# Revit family: 879-002X99-001-DN65-250
name_source: partatom
category: Pipe Accessories
units: mm (PartAtom-declared; Revit-internal decimal feet)

## family parameters
Always vertical = Yes
Cut with Voids When Loaded = No
Part Type = Valve - Breaks Into
Round Connector Dimension = Use Diameter
Shared = No
Work Plane-Based = No

## types (48) — shared parameters
879-0065-00-14400209999 = DN65_PN10/16
879-0065-00-144002099A0 = DN65_PN10/16
879-0065-00-14400219999 = DN65_PN10/16
879-0065-00-144002199A0 = DN65_PN10/16
879-0065-00-14400229999 = DN65_PN10/16
879-0065-00-144002299A0 = DN65_PN10/16
879-0080-00-14400209999 = DN80_PN10/16
879-0080-00-144002099A0 = DN80_PN10/16
879-0080-00-14400219999 = DN80_PN10/16
879-0080-00-144002199A0 = DN80_PN10/16
879-0080-00-14400229999 = DN80_PN10/16
879-0080-00-144002299A0 = DN80_PN10/16
879-0100-00-14400209999 = DN100_PN10/16
879-0100-00-144002099A0 = DN100_PN10/16
879-0100-00-14400219999 = DN100_PN10/16
879-0100-00-144002199A0 = DN100_PN10/16
879-0100-00-14400229990 = DN100_PN10/16
879-0100-00-144002299A0 = DN100_PN10/16
879-0125-00-14400209999 = DN125_PN10/16
879-0125-00-144002099A0 = DN125_PN10/16
879-0125-00-14400219990 = DN125_PN10/16
879-0125-00-144002199A0 = DN125_PN10/16
879-0125-00-14400229999 = DN125_PN10/16
879-0125-00-144002299A0 = DN125_PN10/16
879-0150-00-14400209999 = DN150_PN10/16
879-0150-00-144002099A0 = DN150_PN10/16
879-0150-00-14400219999 = DN150_PN10/16
879-0150-00-144002199A0 = DN150_PN10/16
879-0150-00-14400229999 = DN150_PN10/16
879-0150-00-144002299A0 = DN150_PN10/16
879-0150-00-14400239999 = DN150_PN10/16
879-0150-00-144002399A0 = DN150_PN10/16
879-0200-00-14400209999 = DN200_PN16
879-0200-00-144002099A0 = DN200_PN16
879-0200-00-14400219999 = DN200_PN16
879-0200-00-144002199A0 = DN200_PN16
879-0200-00-14400229999 = DN200_PN16
879-0200-00-144002299A0 = DN200_PN16
879-0200-00-14400239999 = DN200_PN16
879-0200-00-144002399A0 = DN200_PN16
879-0250-00-14400209999 = DN250_PN16
879-0250-00-144002099A0 = DN250_PN16
879-0250-00-14400219999 = DN250_PN16
879-0250-00-144002199A0 = DN250_PN16
879-0250-00-14400229999 = DN250_PN16
879-0250-00-144002299A0 = DN250_PN16
879-0250-00-14400239999 = DN250_PN16
879-0250-00-144002399A0 = DN250_PN16
Body_wall_thickness = 10 mm  [stored 0.0328084 ft]
Description_ = AVK CONSTANT FLOW CONTROL VALVE
Search_Table = 879-002X99-001-DN65-250
URL product pages = https://www.avkvalves.com

## per-type parameters (varying)
- 879-0065-00-14400209999_DN65_PN10/16: Body_Collar_Dia=30.21 mm; Body_Collar_Dia_2=26.01 mm; Body_Flange_Dia=93.55 mm; Body_Flange_Dia_2=103.57 mm; Body_Height_1=72.5 mm; Body_Height_2=36.25 mm; Body_Height_3=58 mm; Body_Height_4=51.25 mm; Body_Top_Dia=13 mm; Body_Top_Dia_2=10.84 mm; Body_With_Dia=72.5 mm; Body_With_Dia_2=78.38 mm; Bolt_support=193.33 mm; Bolt_support_2=96.67 mm; Bolt_support_Dia=12 mm  [stored 0.0393701 ft]; Bolt_support_lenght=52.5 mm; Bolt_support_lenght_2=62.5 mm; Bottom_profile=16.25 mm  [stored 0.0533136 ft]; D1=59 mm; DN=65 mm; FOD=92.5 mm; Fillet_Length=6 mm  [stored 0.019685 ft]; Flange_thickness=19 mm; H3=420 mm; ID=32.5 mm; L=290 mm; L1=307 mm; L_Ref=298.5 mm; PG_Dia=32.5 mm; PG_Ref=48.33 mm; PG_depth=8.4 mm  [stored 0.0275591 ft]; PG_ref=42.5 mm; Pilot_Dia_1=17.5 mm; Pilot_Dia_2=35 mm; Pilot_Dia_3=11.67 mm; Pilot_Dia_4=5.83 mm; Pilot_Dia_5=3.89 mm; Pilot_top_1=264.63 mm; Pilot_top_ref=62.88 mm; Profile1_Height=152 mm; Profile1_Length=25 mm; Profile1_Length_2=16.67 mm; Profile_Dia=6 mm  [stored 0.019685 ft]; Profile_Dia_2=6 mm  [stored 0.019685 ft]; Profile_Dia_3=12 mm  [stored 0.0393701 ft]; Top_Profile=116 mm; Top_Profile_Ref=121 mm; Top_Ref=201.75 mm; Top_Ref_2=233.19 mm; W=255 mm; W_Ref=252 mm
- 879-0065-00-144002099A0_DN65_PN10/16: Body_Collar_Dia=30.21 mm; Body_Collar_Dia_2=26.01 mm; Body_Flange_Dia=93.55 mm; Body_Flange_Dia_2=103.57 mm; Body_Height_1=72.5 mm; Body_Height_2=36.25 mm; Body_Height_3=72.5 mm; Body_Height_4=51.25 mm; Body_Top_Dia=13 mm; Body_Top_Dia_2=10.84 mm; Body_With_Dia=72.5 mm; Body_With_Dia_2=78.38 mm; Bolt_support=193.33 mm; Bolt_support_2=96.67 mm; Bolt_support_Dia=12 mm  [stored 0.0393701 ft]; Bolt_support_lenght=52.55 mm; Bolt_support_lenght_2=62.55 mm; Bottom_profile=16.28 mm; D1=59 mm; DN=65.1 mm; FOD=92.5 mm; Fillet_Length=6 mm  [stored 0.019685 ft]; Flange_thickness=19 mm; H3=420 mm; ID=32.55 mm; L=290 mm; L1=307 mm; L_Ref=298.5 mm; PG_Dia=32.55 mm; PG_Ref=48.33 mm; PG_depth=8.4 mm  [stored 0.0275591 ft]; PG_ref=42.55 mm; Pilot_Dia_1=17.5 mm; Pilot_Dia_2=35 mm; Pilot_Dia_3=11.67 mm; Pilot_Dia_4=5.83 mm; Pilot_Dia_5=3.89 mm; Pilot_top_1=271.88 mm; Pilot_top_ref=55.63 mm; Profile1_Height=170 mm; Profile1_Length=25 mm; Profile1_Length_2=16.67 mm; Profile_Dia=6 mm  [stored 0.019685 ft]; Profile_Dia_2=6 mm  [stored 0.019685 ft]; Profile_Dia_3=12 mm  [stored 0.0393701 ft]; Top_Profile=116 mm; Top_Profile_Ref=121 mm; Top_Ref=216.25 mm; Top_Ref_2=244.06 mm; W=255 mm; W_Ref=252 mm
- 879-0065-00-14400219999_DN65_PN10/16: Body_Collar_Dia=30.21 mm; Body_Collar_Dia_2=26.01 mm; Body_Flange_Dia=93.55 mm; Body_Flange_Dia_2=103.57 mm; Body_Height_1=72.5 mm; Body_Height_2=36.25 mm; Body_Height_3=58 mm; Body_Height_4=51.25 mm; Body_Top_Dia=13 mm; Body_Top_Dia_2=10.84 mm; Body_With_Dia=72.5 mm; Body_With_Dia_2=78.38 mm; Bolt_support=193.33 mm; Bolt_support_2=96.67 mm; Bolt_support_Dia=12 mm  [stored 0.0393701 ft]; Bolt_support_lenght=52.6 mm; Bolt_support_lenght_2=62.6 mm; Bottom_profile=16.3 mm; D1=59 mm; DN=65.2 mm; FOD=92.5 mm; Fillet_Length=6 mm  [stored 0.019685 ft]; Flange_thickness=19 mm; H3=420 mm; ID=32.6 mm; L=290 mm; L1=307 mm; L_Ref=298.5 mm; PG_Dia=32.6 mm; PG_Ref=48.33 mm; PG_depth=8.4 mm  [stored 0.0275591 ft]; PG_ref=42.6 mm; Pilot_Dia_1=17.5 mm; Pilot_Dia_2=35 mm; Pilot_Dia_3=11.67 mm; Pilot_Dia_4=5.83 mm; Pilot_Dia_5=3.89 mm; Pilot_top_1=264.63 mm; Pilot_top_ref=62.88 mm; Profile1_Height=152 mm; Profile1_Length=25 mm; Profile1_Length_2=16.67 mm; Profile_Dia=6 mm  [stored 0.019685 ft]; Profile_Dia_2=6 mm  [stored 0.019685 ft]; Profile_Dia_3=12 mm  [stored 0.0393701 ft]; Top_Profile=116 mm; Top_Profile_Ref=121 mm; Top_Ref=201.75 mm; Top_Ref_2=233.19 mm; W=255 mm; W_Ref=252 mm
- 879-0065-00-144002199A0_DN65_PN10/16: Body_Collar_Dia=30.21 mm; Body_Collar_Dia_2=26.01 mm; Body_Flange_Dia=93.55 mm; Body_Flange_Dia_2=103.57 mm; Body_Height_1=72.5 mm; Body_Height_2=36.25 mm; Body_Height_3=72.5 mm; Body_Height_4=51.25 mm; Body_Top_Dia=13 mm; Body_Top_Dia_2=10.84 mm; Body_With_Dia=72.5 mm; Body_With_Dia_2=78.38 mm; Bolt_support=193.33 mm; Bolt_support_2=96.67 mm; Bolt_support_Dia=12 mm  [stored 0.0393701 ft]; Bolt_support_lenght=52.65 mm; Bolt_support_lenght_2=62.65 mm; Bottom_profile=16.33 mm; D1=59 mm; DN=65.3 mm; FOD=92.5 mm; Fillet_Length=6 mm  [stored 0.019685 ft]; Flange_thickness=19 mm; H3=420 mm; ID=32.65 mm; L=290 mm; L1=307 mm; L_Ref=298.5 mm; PG_Dia=32.65 mm; PG_Ref=48.33 mm; PG_depth=8.4 mm  [stored 0.0275591 ft]; PG_ref=42.65 mm; Pilot_Dia_1=17.5 mm; Pilot_Dia_2=35 mm; Pilot_Dia_3=11.67 mm; Pilot_Dia_4=5.83 mm; Pilot_Dia_5=3.89 mm; Pilot_top_1=271.88 mm; Pilot_top_ref=55.63 mm; Profile1_Height=170 mm; Profile1_Length=25 mm; Profile1_Length_2=16.67 mm; Profile_Dia=6 mm  [stored 0.019685 ft]; Profile_Dia_2=6 mm  [stored 0.019685 ft]; Profile_Dia_3=12 mm  [stored 0.0393701 ft]; Top_Profile=116 mm; Top_Profile_Ref=121 mm; Top_Ref=216.25 mm; Top_Ref_2=244.06 mm; W=255 mm; W_Ref=252 mm
- 879-0065-00-14400229999_DN65_PN10/16: Body_Collar_Dia=30.21 mm; Body_Collar_Dia_2=26.01 mm; Body_Flange_Dia=93.55 mm; Body_Flange_Dia_2=103.57 mm; Body_Height_1=72.5 mm; Body_Height_2=36.25 mm; Body_Height_3=58 mm; Body_Height_4=51.25 mm; Body_Top_Dia=13 mm; Body_Top_Dia_2=10.84 mm; Body_With_Dia=72.5 mm; Body_With_Dia_2=78.38 mm; Bolt_support=193.33 mm; Bolt_support_2=96.67 mm; Bolt_support_Dia=12 mm  [stored 0.0393701 ft]; Bolt_support_lenght=52.7 mm; Bolt_support_lenght_2=62.7 mm; Bottom_profile=16.35 mm  [stored 0.0536417 ft]; D1=59 mm; DN=65.4 mm; FOD=92.5 mm; Fillet_Length=6 mm  [stored 0.019685 ft]; Flange_thickness=19 mm; H3=420 mm; ID=32.7 mm; L=290 mm; L1=307 mm; L_Ref=298.5 mm; PG_Dia=32.7 mm; PG_Ref=48.33 mm; PG_depth=8.4 mm  [stored 0.0275591 ft]; PG_ref=42.7 mm; Pilot_Dia_1=17.5 mm; Pilot_Dia_2=35 mm; Pilot_Dia_3=11.67 mm; Pilot_Dia_4=5.83 mm; Pilot_Dia_5=3.89 mm; Pilot_top_1=264.63 mm; Pilot_top_ref=62.88 mm; Profile1_Height=152 mm; Profile1_Length=25 mm; Profile1_Length_2=16.67 mm; Profile_Dia=6 mm  [stored 0.019685 ft]; Profile_Dia_2=6 mm  [stored 0.019685 ft]; Profile_Dia_3=12 mm  [stored 0.0393701 ft]; Top_Profile=116 mm; Top_Profile_Ref=121 mm; Top_Ref=201.75 mm; Top_Ref_2=233.19 mm; W=255 mm; W_Ref=252 mm
- 879-0065-00-144002299A0_DN65_PN10/16: Body_Collar_Dia=30.21 mm; Body_Collar_Dia_2=26.01 mm; Body_Flange_Dia=93.55 mm; Body_Flange_Dia_2=103.57 mm; Body_Height_1=72.5 mm; Body_Height_2=36.25 mm; Body_Height_3=72.5 mm; Body_Height_4=51.25 mm; Body_Top_Dia=13 mm; Body_Top_Dia_2=10.84 mm; Body_With_Dia=72.5 mm; Body_With_Dia_2=78.38 mm; Bolt_support=193.33 mm; Bolt_support_2=96.67 mm; Bolt_support_Dia=12 mm  [stored 0.0393701 ft]; Bolt_support_lenght=52.75 mm; Bolt_support_lenght_2=62.75 mm; Bottom_profile=16.38 mm; D1=59 mm; DN=65.5 mm; FOD=92.5 mm; Fillet_Length=6 mm  [stored 0.019685 ft]; Flange_thickness=19 mm; H3=420 mm; ID=32.75 mm; L=290 mm; L1=307 mm; L_Ref=298.5 mm; PG_Dia=32.75 mm; PG_Ref=48.33 mm; PG_depth=8.4 mm  [stored 0.0275591 ft]; PG_ref=42.75 mm; Pilot_Dia_1=17.5 mm; Pilot_Dia_2=35 mm; Pilot_Dia_3=11.67 mm; Pilot_Dia_4=5.83 mm; Pilot_Dia_5=3.89 mm; Pilot_top_1=271.88 mm; Pilot_top_ref=55.63 mm; Profile1_Height=170 mm; Profile1_Length=25 mm; Profile1_Length_2=16.67 mm; Profile_Dia=6 mm  [stored 0.019685 ft]; Profile_Dia_2=6 mm  [stored 0.019685 ft]; Profile_Dia_3=12 mm  [stored 0.0393701 ft]; Top_Profile=116 mm; Top_Profile_Ref=121 mm; Top_Ref=216.25 mm; Top_Ref_2=244.06 mm; W=255 mm; W_Ref=252 mm
- 879-0080-00-14400209999_DN80_PN10/16: Body_Collar_Dia=32.29 mm; Body_Collar_Dia_2=27.8 mm; Body_Flange_Dia=100 mm; Body_Flange_Dia_2=110.71 mm; Body_Height_1=77.5 mm; Body_Height_2=38.75 mm; Body_Height_3=62 mm; Body_Height_4=53.75 mm; Body_Top_Dia=13.9 mm; Body_Top_Dia_2=11.58 mm; Body_With_Dia=77.5 mm; Body_With_Dia_2=83.78 mm; Bolt_support=206.67 mm; Bolt_support_2=103.33 mm; Bolt_support_Dia=12 mm  [stored 0.0393701 ft]; Bolt_support_lenght=60 mm; Bolt_support_lenght_2=70 mm; Bottom_profile=20 mm; D1=66 mm; DN=80 mm; FOD=100 mm; Fillet_Length=6 mm  [stored 0.019685 ft]; Flange_thickness=19 mm; H3=435 mm; ID=40 mm; L=310 mm; L1=327 mm; L_Ref=318.5 mm; PG_Dia=40 mm; PG_Ref=51.67 mm; PG_depth=8.4 mm  [stored 0.0275591 ft]; PG_ref=50 mm; Pilot_Dia_1=19.5 mm; Pilot_Dia_2=39 mm; Pilot_Dia_3=13 mm; Pilot_Dia_4=6.5 mm; Pilot_Dia_5=4.33 mm; Pilot_top_1=274.13 mm; Pilot_top_ref=60.88 mm; Profile1_Height=179 mm; Profile1_Length=27.03 mm; Profile1_Length_2=18.02 mm; Profile_Dia=6 mm  [stored 0.019685 ft]; Profile_Dia_2=6 mm  [stored 0.019685 ft]; Profile_Dia_3=12 mm  [stored 0.0393701 ft]; Top_Profile=124 mm; Top_Profile_Ref=129 mm; Top_Ref=213.25 mm; Top_Ref_2=243.69 mm; W=270 mm; W_Ref=267 mm
- 879-0080-00-144002099A0_DN80_PN10/16: Body_Collar_Dia=32.29 mm; Body_Collar_Dia_2=27.8 mm; Body_Flange_Dia=100 mm; Body_Flange_Dia_2=110.71 mm; Body_Height_1=77.5 mm; Body_Height_2=38.75 mm; Body_Height_3=77.5 mm; Body_Height_4=53.75 mm; Body_Top_Dia=13.9 mm; Body_Top_Dia_2=11.58 mm; Body_With_Dia=77.5 mm; Body_With_Dia_2=83.78 mm; Bolt_support=206.67 mm; Bolt_support_2=103.33 mm; Bolt_support_Dia=12 mm  [stored 0.0393701 ft]; Bolt_support_lenght=60.05 mm; Bolt_support_lenght_2=70.05 mm; Bottom_profile=20.03 mm; D1=66 mm; DN=80.1 mm; FOD=100 mm; Fillet_Length=6 mm  [stored 0.019685 ft]; Flange_thickness=19 mm; H3=435 mm; ID=40.05 mm; L=310 mm; L1=327 mm; L_Ref=318.5 mm; PG_Dia=40.05 mm; PG_Ref=51.67 mm; PG_depth=8.4 mm  [stored 0.0275591 ft]; PG_ref=50.05 mm; Pilot_Dia_1=19.5 mm; Pilot_Dia_2=39 mm; Pilot_Dia_3=13 mm; Pilot_Dia_4=6.5 mm; Pilot_Dia_5=4.33 mm; Pilot_top_1=281.88 mm; Pilot_top_ref=53.13 mm; Profile1_Height=168 mm; Profile1_Length=27.03 mm; Profile1_Length_2=18.02 mm; Profile_Dia=6 mm  [stored 0.019685 ft]; Profile_Dia_2=6 mm  [stored 0.019685 ft]; Profile_Dia_3=12 mm  [stored 0.0393701 ft]; Top_Profile=124 mm; Top_Profile_Ref=129 mm; Top_Ref=228.75 mm; Top_Ref_2=255.31 mm; W=270 mm; W_Ref=267 mm
- 879-0080-00-14400219999_DN80_PN10/16: Body_Collar_Dia=32.29 mm; Body_Collar_Dia_2=27.8 mm; Body_Flange_Dia=100 mm; Body_Flange_Dia_2=110.71 mm; Body_Height_1=77.5 mm; Body_Height_2=38.75 mm; Body_Height_3=62 mm; Body_Height_4=53.75 mm; Body_Top_Dia=13.9 mm; Body_Top_Dia_2=11.58 mm; Body_With_Dia=77.5 mm; Body_With_Dia_2=83.78 mm; Bolt_support=206.67 mm; Bolt_support_2=103.33 mm; Bolt_support_Dia=12 mm  [stored 0.0393701 ft]; Bolt_support_lenght=60.1 mm; Bolt_support_lenght_2=70.1 mm; Bottom_profile=20.05 mm; D1=66 mm; DN=80.2 mm; FOD=100 mm; Fillet_Length=6 mm  [stored 0.019685 ft]; Flange_thickness=19 mm; H3=435 mm; ID=40.1 mm; L=310 mm; L1=327 mm; L_Ref=318.5 mm; PG_Dia=40.1 mm; PG_Ref=51.67 mm; PG_depth=8.4 mm  [stored 0.0275591 ft]; PG_ref=50.1 mm; Pilot_Dia_1=19.5 mm; Pilot_Dia_2=39 mm; Pilot_Dia_3=13 mm; Pilot_Dia_4=6.5 mm; Pilot_Dia_5=4.33 mm; Pilot_top_1=274.13 mm; Pilot_top_ref=60.88 mm; Profile1_Height=179 mm; Profile1_Length=27.03 mm; Profile1_Length_2=18.02 mm; Profile_Dia=6 mm  [stored 0.019685 ft]; Profile_Dia_2=6 mm  [stored 0.019685 ft]; Profile_Dia_3=12 mm  [stored 0.0393701 ft]; Top_Profile=124 mm; Top_Profile_Ref=129 mm; Top_Ref=213.25 mm; Top_Ref_2=243.69 mm; W=270 mm; W_Ref=267 mm
- 879-0080-00-144002199A0_DN80_PN10/16: Body_Collar_Dia=32.29 mm; Body_Collar_Dia_2=27.8 mm; Body_Flange_Dia=100 mm; Body_Flange_Dia_2=110.71 mm; Body_Height_1=77.5 mm; Body_Height_2=38.75 mm; Body_Height_3=77.5 mm; Body_Height_4=53.75 mm; Body_Top_Dia=13.9 mm; Body_Top_Dia_2=11.58 mm; Body_With_Dia=77.5 mm; Body_With_Dia_2=83.78 mm; Bolt_support=206.67 mm; Bolt_support_2=103.33 mm; Bolt_support_Dia=12 mm  [stored 0.0393701 ft]; Bolt_support_lenght=60.15 mm; Bolt_support_lenght_2=70.15 mm; Bottom_profile=20.08 mm; D1=66 mm; DN=80.3 mm; FOD=100 mm; Fillet_Length=6 mm  [stored 0.019685 ft]; Flange_thickness=19 mm; H3=435 mm; ID=40.15 mm; L=310 mm; L1=327 mm; L_Ref=318.5 mm; PG_Dia=40.15 mm; PG_Ref=51.67 mm; PG_depth=8.4 mm  [stored 0.0275591 ft]; PG_ref=50.15 mm; Pilot_Dia_1=19.5 mm; Pilot_Dia_2=39 mm; Pilot_Dia_3=13 mm; Pilot_Dia_4=6.5 mm; Pilot_Dia_5=4.33 mm; Pilot_top_1=281.88 mm; Pilot_top_ref=53.13 mm; Profile1_Height=168 mm; Profile1_Length=27.03 mm; Profile1_Length_2=18.02 mm; Profile_Dia=6 mm  [stored 0.019685 ft]; Profile_Dia_2=6 mm  [stored 0.019685 ft]; Profile_Dia_3=12 mm  [stored 0.0393701 ft]; Top_Profile=124 mm; Top_Profile_Ref=129 mm; Top_Ref=228.75 mm; Top_Ref_2=255.31 mm; W=270 mm; W_Ref=267 mm
- 879-0080-00-14400229999_DN80_PN10/16: Body_Collar_Dia=32.29 mm; Body_Collar_Dia_2=27.8 mm; Body_Flange_Dia=100 mm; Body_Flange_Dia_2=110.71 mm; Body_Height_1=77.5 mm; Body_Height_2=38.75 mm; Body_Height_3=62 mm; Body_Height_4=53.75 mm; Body_Top_Dia=13.9 mm; Body_Top_Dia_2=11.58 mm; Body_With_Dia=77.5 mm; Body_With_Dia_2=83.78 mm; Bolt_support=206.67 mm; Bolt_support_2=103.33 mm; Bolt_support_Dia=12 mm  [stored 0.0393701 ft]; Bolt_support_lenght=60.2 mm; Bolt_support_lenght_2=70.2 mm; Bottom_profile=20.1 mm; D1=66 mm; DN=80.4 mm; FOD=100 mm; Fillet_Length=6 mm  [stored 0.019685 ft]; Flange_thickness=19 mm; H3=435 mm; ID=40.2 mm; L=310 mm; L1=327 mm; L_Ref=318.5 mm; PG_Dia=40.2 mm; PG_Ref=51.67 mm; PG_depth=8.4 mm  [stored 0.0275591 ft]; PG_ref=50.2 mm; Pilot_Dia_1=19.5 mm; Pilot_Dia_2=39 mm; Pilot_Dia_3=13 mm; Pilot_Dia_4=6.5 mm; Pilot_Dia_5=4.33 mm; Pilot_top_1=274.13 mm; Pilot_top_ref=60.88 mm; Profile1_Height=179 mm; Profile1_Length=27.03 mm; Profile1_Length_2=18.02 mm; Profile_Dia=6 mm  [stored 0.019685 ft]; Profile_Dia_2=6 mm  [stored 0.019685 ft]; Profile_Dia_3=12 mm  [stored 0.0393701 ft]; Top_Profile=124 mm; Top_Profile_Ref=129 mm; Top_Ref=213.25 mm; Top_Ref_2=243.69 mm; W=270 mm; W_Ref=267 mm
- 879-0080-00-144002299A0_DN80_PN10/16: Body_Collar_Dia=32.29 mm; Body_Collar_Dia_2=27.8 mm; Body_Flange_Dia=100 mm; Body_Flange_Dia_2=110.71 mm; Body_Height_1=77.5 mm; Body_Height_2=38.75 mm; Body_Height_3=77.5 mm; Body_Height_4=53.75 mm; Body_Top_Dia=13.9 mm; Body_Top_Dia_2=11.58 mm; Body_With_Dia=77.5 mm; Body_With_Dia_2=83.78 mm; Bolt_support=206.67 mm; Bolt_support_2=103.33 mm; Bolt_support_Dia=12 mm  [stored 0.0393701 ft]; Bolt_support_lenght=60.25 mm; Bolt_support_lenght_2=70.25 mm; Bottom_profile=20.13 mm; D1=66 mm; DN=80.5 mm; FOD=100 mm; Fillet_Length=6 mm  [stored 0.019685 ft]; Flange_thickness=19 mm; H3=435 mm; ID=40.25 mm; L=310 mm; L1=327 mm; L_Ref=318.5 mm; PG_Dia=40.25 mm; PG_Ref=51.67 mm; PG_depth=8.4 mm  [stored 0.0275591 ft]; PG_ref=50.25 mm; Pilot_Dia_1=19.5 mm; Pilot_Dia_2=39 mm; Pilot_Dia_3=13 mm; Pilot_Dia_4=6.5 mm; Pilot_Dia_5=4.33 mm; Pilot_top_1=281.88 mm; Pilot_top_ref=53.13 mm; Profile1_Height=168 mm; Profile1_Length=27.03 mm; Profile1_Length_2=18.02 mm; Profile_Dia=6 mm  [stored 0.019685 ft]; Profile_Dia_2=6 mm  [stored 0.019685 ft]; Profile_Dia_3=12 mm  [stored 0.0393701 ft]; Top_Profile=124 mm; Top_Profile_Ref=129 mm; Top_Ref=228.75 mm; Top_Ref_2=255.31 mm; W=270 mm; W_Ref=267 mm
- 879-0100-00-14400209999_DN100_PN10/16: Body_Collar_Dia=36.46 mm; Body_Collar_Dia_2=31.39 mm; Body_Flange_Dia=112.9 mm; Body_Flange_Dia_2=125 mm; Body_Height_1=87.5 mm; Body_Height_2=43.75 mm; Body_Height_3=58.5 mm; Body_Height_4=58.75 mm; Body_Top_Dia=15.7 mm; Body_Top_Dia_2=13.08 mm; Body_With_Dia=87.5 mm; Body_With_Dia_2=94.59 mm; Bolt_support=233.33 mm; Bolt_support_2=116.67 mm; Bolt_support_Dia=12 mm  [stored 0.0393701 ft]; Bolt_support_lenght=70 mm; Bolt_support_lenght_2=80 mm; Bottom_profile=25 mm; D1=78 mm; DN=100 mm; FOD=110 mm; Fillet_Length=6 mm  [stored 0.019685 ft]; Flange_thickness=19 mm; H3=450 mm; ID=50 mm; L=350 mm; L1=367 mm; L_Ref=358.5 mm; PG_Dia=50 mm; PG_Ref=58.33 mm; PG_depth=8.4 mm  [stored 0.0275591 ft]; PG_ref=60 mm; Pilot_Dia_1=22 mm; Pilot_Dia_2=44 mm; Pilot_Dia_3=14.67 mm; Pilot_Dia_4=7.33 mm; Pilot_Dia_5=4.89 mm; Pilot_top_1=282.38 mm; Pilot_top_ref=57.63 mm; Profile1_Height=185 mm; Profile1_Length=29.73 mm; Profile1_Length_2=19.82 mm; Profile_Dia=6 mm  [stored 0.019685 ft]; Profile_Dia_2=6 mm  [stored 0.019685 ft]; Profile_Dia_3=12 mm  [stored 0.0393701 ft]; Top_Profile=140 mm; Top_Profile_Ref=145 mm; Top_Ref=224.75 mm; Top_Ref_2=253.56 mm; W=290 mm; W_Ref=287 mm
- 879-0100-00-144002099A0_DN100_PN10/16: Body_Collar_Dia=36.46 mm; Body_Collar_Dia_2=31.39 mm; Body_Flange_Dia=112.9 mm; Body_Flange_Dia_2=125 mm; Body_Height_1=87.5 mm; Body_Height_2=43.75 mm; Body_Height_3=70 mm; Body_Height_4=58.75 mm; Body_Top_Dia=15.7 mm; Body_Top_Dia_2=13.08 mm; Body_With_Dia=87.5 mm; Body_With_Dia_2=94.59 mm; Bolt_support=233.33 mm; Bolt_support_2=116.67 mm; Bolt_support_Dia=12 mm  [stored 0.0393701 ft]; Bolt_support_lenght=70.05 mm; Bolt_support_lenght_2=80.05 mm; Bottom_profile=25.03 mm; D1=78 mm; DN=100.1 mm; FOD=110 mm; Fillet_Length=6 mm  [stored 0.019685 ft]; Flange_thickness=19 mm; H3=450 mm; ID=50.05 mm; L=350 mm; L1=367 mm; L_Ref=358.5 mm; PG_Dia=50.05 mm; PG_Ref=58.33 mm; PG_depth=8.4 mm  [stored 0.0275591 ft]; PG_ref=60.05 mm; Pilot_Dia_1=22 mm; Pilot_Dia_2=44 mm; Pilot_Dia_3=14.67 mm; Pilot_Dia_4=7.33 mm; Pilot_Dia_5=4.89 mm; Pilot_top_1=288.13 mm; Pilot_top_ref=51.88 mm; Profile1_Height=176 mm; Profile1_Length=29.73 mm; Profile1_Length_2=19.82 mm; Profile_Dia=6 mm  [stored 0.019685 ft]; Profile_Dia_2=6 mm  [stored 0.019685 ft]; Profile_Dia_3=12 mm  [stored 0.0393701 ft]; Top_Profile=140 mm; Top_Profile_Ref=145 mm; Top_Ref=236.25 mm; Top_Ref_2=262.19 mm; W=290 mm; W_Ref=287 mm
- 879-0100-00-14400219999_DN100_PN10/16: Body_Collar_Dia=36.46 mm; Body_Collar_Dia_2=31.39 mm; Body_Flange_Dia=112.9 mm; Body_Flange_Dia_2=125 mm; Body_Height_1=87.5 mm; Body_Height_2=43.75 mm; Body_Height_3=58.5 mm; Body_Height_4=58.75 mm; Body_Top_Dia=15.7 mm; Body_Top_Dia_2=13.08 mm; Body_With_Dia=87.5 mm; Body_With_Dia_2=94.59 mm; Bolt_support=233.33 mm; Bolt_support_2=116.67 mm; Bolt_support_Dia=12 mm  [stored 0.0393701 ft]; Bolt_support_lenght=70.1 mm; Bolt_support_lenght_2=80.1 mm; Bottom_profile=25.05 mm; D1=78 mm; DN=100.2 mm; FOD=110 mm; Fillet_Length=6 mm  [stored 0.019685 ft]; Flange_thickness=19 mm; H3=450 mm; ID=50.1 mm; L=350 mm; L1=367 mm; L_Ref=358.5 mm; PG_Dia=50.1 mm; PG_Ref=58.33 mm; PG_depth=8.4 mm  [stored 0.0275591 ft]; PG_ref=60.1 mm; Pilot_Dia_1=22 mm; Pilot_Dia_2=44 mm; Pilot_Dia_3=14.67 mm; Pilot_Dia_4=7.33 mm; Pilot_Dia_5=4.89 mm; Pilot_top_1=282.38 mm; Pilot_top_ref=57.63 mm; Profile1_Height=185 mm; Profile1_Length=29.73 mm; Profile1_Length_2=19.82 mm; Profile_Dia=6 mm  [stored 0.019685 ft]; Profile_Dia_2=6 mm  [stored 0.019685 ft]; Profile_Dia_3=12 mm  [stored 0.0393701 ft]; Top_Profile=140 mm; Top_Profile_Ref=145 mm; Top_Ref=224.75 mm; Top_Ref_2=253.56 mm; W=290 mm; W_Ref=287 mm
- 879-0100-00-144002199A0_DN100_PN10/16: Body_Collar_Dia=36.46 mm; Body_Collar_Dia_2=31.39 mm; Body_Flange_Dia=112.9 mm; Body_Flange_Dia_2=125 mm; Body_Height_1=87.5 mm; Body_Height_2=43.75 mm; Body_Height_3=70 mm; Body_Height_4=58.75 mm; Body_Top_Dia=15.7 mm; Body_Top_Dia_2=13.08 mm; Body_With_Dia=87.5 mm; Body_With_Dia_2=94.59 mm; Bolt_support=233.33 mm; Bolt_support_2=116.67 mm; Bolt_support_Dia=12 mm  [stored 0.0393701 ft]; Bolt_support_lenght=70.15 mm; Bolt_support_lenght_2=80.15 mm; Bottom_profile=25.08 mm; D1=78 mm; DN=100.3 mm; FOD=110 mm; Fillet_Length=6 mm  [stored 0.019685 ft]; Flange_thickness=19 mm; H3=450 mm; ID=50.15 mm; L=350 mm; L1=367 mm; L_Ref=358.5 mm; PG_Dia=50.15 mm; PG_Ref=58.33 mm; PG_depth=8.4 mm  [stored 0.0275591 ft]; PG_ref=60.15 mm; Pilot_Dia_1=22 mm; Pilot_Dia_2=44 mm; Pilot_Dia_3=14.67 mm; Pilot_Dia_4=7.33 mm; Pilot_Dia_5=4.89 mm; Pilot_top_1=288.13 mm; Pilot_top_ref=51.88 mm; Profile1_Height=176 mm; Profile1_Length=29.73 mm; Profile1_Length_2=19.82 mm; Profile_Dia=6 mm  [stored 0.019685 ft]; Profile_Dia_2=6 mm  [stored 0.019685 ft]; Profile_Dia_3=12 mm  [stored 0.0393701 ft]; Top_Profile=140 mm; Top_Profile_Ref=145 mm; Top_Ref=236.25 mm; Top_Ref_2=262.19 mm; W=290 mm; W_Ref=287 mm
- 879-0100-00-14400229990_DN100_PN10/16: Body_Collar_Dia=36.46 mm; Body_Collar_Dia_2=31.39 mm; Body_Flange_Dia=112.9 mm; Body_Flange_Dia_2=125 mm; Body_Height_1=87.5 mm; Body_Height_2=43.75 mm; Body_Height_3=58.5 mm; Body_Height_4=58.75 mm; Body_Top_Dia=15.7 mm; Body_Top_Dia_2=13.08 mm; Body_With_Dia=87.5 mm; Body_With_Dia_2=94.59 mm; Bolt_support=233.33 mm; Bolt_support_2=116.67 mm; Bolt_support_Dia=12 mm  [stored 0.0393701 ft]; Bolt_support_lenght=70.2 mm; Bolt_support_lenght_2=80.2 mm; Bottom_profile=25.1 mm; D1=78 mm; DN=100.4 mm; FOD=110 mm; Fillet_Length=6 mm  [stored 0.019685 ft]; Flange_thickness=19 mm; H3=450 mm; ID=50.2 mm; L=350 mm; L1=367 mm; L_Ref=358.5 mm; PG_Dia=50.2 mm; PG_Ref=58.33 mm; PG_depth=8.4 mm  [stored 0.0275591 ft]; PG_ref=60.2 mm; Pilot_Dia_1=22 mm; Pilot_Dia_2=44 mm; Pilot_Dia_3=14.67 mm; Pilot_Dia_4=7.33 mm; Pilot_Dia_5=4.89 mm; Pilot_top_1=282.38 mm; Pilot_top_ref=57.63 mm; Profile1_Height=185 mm; Profile1_Length=29.73 mm; Profile1_Length_2=19.82 mm; Profile_Dia=6 mm  [stored 0.019685 ft]; Profile_Dia_2=6 mm  [stored 0.019685 ft]; Profile_Dia_3=12 mm  [stored 0.0393701 ft]; Top_Profile=140 mm; Top_Profile_Ref=145 mm; Top_Ref=224.75 mm; Top_Ref_2=253.56 mm; W=290 mm; W_Ref=287 mm
- 879-0100-00-144002299A0_DN100_PN10/16: Body_Collar_Dia=36.46 mm; Body_Collar_Dia_2=31.39 mm; Body_Flange_Dia=112.9 mm; Body_Flange_Dia_2=125 mm; Body_Height_1=87.5 mm; Body_Height_2=43.75 mm; Body_Height_3=70 mm; Body_Height_4=58.75 mm; Body_Top_Dia=15.7 mm; Body_Top_Dia_2=13.08 mm; Body_With_Dia=87.5 mm; Body_With_Dia_2=94.59 mm; Bolt_support=233.33 mm; Bolt_support_2=116.67 mm; Bolt_support_Dia=12 mm  [stored 0.0393701 ft]; Bolt_support_lenght=70.25 mm; Bolt_support_lenght_2=80.25 mm; Bottom_profile=25.13 mm; D1=78 mm; DN=100.5 mm; FOD=110 mm; Fillet_Length=6 mm  [stored 0.019685 ft]; Flange_thickness=19 mm; H3=450 mm; ID=50.25 mm; L=350 mm; L1=367 mm; L_Ref=358.5 mm; PG_Dia=50.25 mm; PG_Ref=58.33 mm; PG_depth=8.4 mm  [stored 0.0275591 ft]; PG_ref=60.25 mm; Pilot_Dia_1=22 mm; Pilot_Dia_2=44 mm; Pilot_Dia_3=14.67 mm; Pilot_Dia_4=7.33 mm; Pilot_Dia_5=4.89 mm; Pilot_top_1=288.13 mm; Pilot_top_ref=51.88 mm; Profile1_Height=176 mm; Profile1_Length=29.73 mm; Profile1_Length_2=19.82 mm; Profile_Dia=6 mm  [stored 0.019685 ft]; Profile_Dia_2=6 mm  [stored 0.019685 ft]; Profile_Dia_3=12 mm  [stored 0.0393701 ft]; Top_Profile=140 mm; Top_Profile_Ref=145 mm; Top_Ref=236.25 mm; Top_Ref_2=262.19 mm; W=290 mm; W_Ref=287 mm
- 879-0125-00-14400209999_DN125_PN10/16: Body_Collar_Dia=41.67 mm; Body_Collar_Dia_2=35.87 mm; Body_Flange_Dia=129.03 mm; Body_Flange_Dia_2=142.86 mm; Body_Height_1=100 mm; Body_Height_2=50 mm; Body_Height_3=58.5 mm; Body_Height_4=65 mm; Body_Top_Dia=17.94 mm; Body_Top_Dia_2=14.95 mm; Body_With_Dia=100 mm; Body_With_Dia_2=108.11 mm; Bolt_support=266.67 mm; Bolt_support_2=133.33 mm; Bolt_support_Dia=12 mm  [stored 0.0393701 ft]; Bolt_support_lenght=82.5 mm; Bolt_support_lenght_2=92.5 mm; Bottom_profile=31.25 mm; D1=92 mm; DN=125 mm; FOD=125 mm; Fillet_Length=6 mm  [stored 0.019685 ft]; Flange_thickness=19 mm; H3=470 mm; ID=62.5 mm; L=400 mm; L1=417 mm; L_Ref=408.5 mm; PG_Dia=62.5 mm; PG_Ref=66.67 mm; PG_depth=8.4 mm  [stored 0.0275591 ft]; PG_ref=72.5 mm; Pilot_Dia_1=27.5 mm; Pilot_Dia_2=55 mm; Pilot_Dia_3=18.33 mm; Pilot_Dia_4=9.17 mm; Pilot_Dia_5=6.11 mm; Pilot_top_1=294.25 mm; Pilot_top_ref=50.75 mm; Profile1_Height=205 mm; Profile1_Length=33.78 mm; Profile1_Length_2=22.52 mm; Profile_Dia=6 mm  [stored 0.019685 ft]; Profile_Dia_2=6 mm  [stored 0.019685 ft]; Profile_Dia_3=12 mm  [stored 0.0393701 ft]; Top_Profile=160 mm; Top_Profile_Ref=165 mm; Top_Ref=243.5 mm; Top_Ref_2=268.88 mm; W=310 mm; W_Ref=307 mm
- 879-0125-00-144002099A0_DN125_PN10/16: Body_Collar_Dia=41.67 mm; Body_Collar_Dia_2=35.87 mm; Body_Flange_Dia=129.03 mm; Body_Flange_Dia_2=142.86 mm; Body_Height_1=100 mm; Body_Height_2=50 mm; Body_Height_3=70 mm; Body_Height_4=65 mm; Body_Top_Dia=17.94 mm; Body_Top_Dia_2=14.95 mm; Body_With_Dia=100 mm; Body_With_Dia_2=108.11 mm; Bolt_support=266.67 mm; Bolt_support_2=133.33 mm; Bolt_support_Dia=12 mm  [stored 0.0393701 ft]; Bolt_support_lenght=82.55 mm; Bolt_support_lenght_2=92.55 mm; Bottom_profile=31.28 mm; D1=92 mm; DN=125.1 mm; FOD=125 mm; Fillet_Length=6 mm  [stored 0.019685 ft]; Flange_thickness=19 mm; H3=470 mm; ID=62.55 mm; L=400 mm; L1=417 mm; L_Ref=408.5 mm; PG_Dia=62.55 mm; PG_Ref=66.67 mm; PG_depth=8.4 mm  [stored 0.0275591 ft]; PG_ref=72.55 mm; Pilot_Dia_1=27.5 mm; Pilot_Dia_2=55 mm; Pilot_Dia_3=18.33 mm; Pilot_Dia_4=9.17 mm; Pilot_Dia_5=6.11 mm; Pilot_top_1=300 mm; Pilot_top_ref=45 mm; Profile1_Height=195 mm; Profile1_Length=33.78 mm; Profile1_Length_2=22.52 mm; Profile_Dia=6 mm  [stored 0.019685 ft]; Profile_Dia_2=6 mm  [stored 0.019685 ft]; Profile_Dia_3=12 mm  [stored 0.0393701 ft]; Top_Profile=160 mm; Top_Profile_Ref=165 mm; Top_Ref=255 mm; Top_Ref_2=277.5 mm; W=310 mm; W_Ref=307 mm
- 879-0125-00-14400219990_DN125_PN10/16: Body_Collar_Dia=41.67 mm; Body_Collar_Dia_2=35.87 mm; Body_Flange_Dia=129.03 mm; Body_Flange_Dia_2=142.86 mm; Body_Height_1=100 mm; Body_Height_2=50 mm; Body_Height_3=58.5 mm; Body_Height_4=65 mm; Body_Top_Dia=17.94 mm; Body_Top_Dia_2=14.95 mm; Body_With_Dia=100 mm; Body_With_Dia_2=108.11 mm; Bolt_support=266.67 mm; Bolt_support_2=133.33 mm; Bolt_support_Dia=12 mm  [stored 0.0393701 ft]; Bolt_support_lenght=82.6 mm; Bolt_support_lenght_2=92.6 mm; Bottom_profile=31.3 mm; D1=92 mm; DN=125.2 mm; FOD=125 mm; Fillet_Length=6 mm  [stored 0.019685 ft]; Flange_thickness=19 mm; H3=470 mm; ID=62.6 mm; L=400 mm; L1=417 mm; L_Ref=408.5 mm; PG_Dia=62.6 mm; PG_Ref=66.67 mm; PG_depth=8.4 mm  [stored 0.0275591 ft]; PG_ref=72.6 mm; Pilot_Dia_1=27.5 mm; Pilot_Dia_2=55 mm; Pilot_Dia_3=18.33 mm; Pilot_Dia_4=9.17 mm; Pilot_Dia_5=6.11 mm; Pilot_top_1=294.25 mm; Pilot_top_ref=50.75 mm; Profile1_Height=205 mm; Profile1_Length=33.78 mm; Profile1_Length_2=22.52 mm; Profile_Dia=6 mm  [stored 0.019685 ft]; Profile_Dia_2=6 mm  [stored 0.019685 ft]; Profile_Dia_3=12 mm  [stored 0.0393701 ft]; Top_Profile=160 mm; Top_Profile_Ref=165 mm; Top_Ref=243.5 mm; Top_Ref_2=268.88 mm; W=310 mm; W_Ref=307 mm
- 879-0125-00-144002199A0_DN125_PN10/16: Body_Collar_Dia=41.67 mm; Body_Collar_Dia_2=35.87 mm; Body_Flange_Dia=129.03 mm; Body_Flange_Dia_2=142.86 mm; Body_Height_1=100 mm; Body_Height_2=50 mm; Body_Height_3=70 mm; Body_Height_4=65 mm; Body_Top_Dia=17.94 mm; Body_Top_Dia_2=14.95 mm; Body_With_Dia=100 mm; Body_With_Dia_2=108.11 mm; Bolt_support=266.67 mm; Bolt_support_2=133.33 mm; Bolt_support_Dia=12 mm  [stored 0.0393701 ft]; Bolt_support_lenght=82.65 mm; Bolt_support_lenght_2=92.65 mm; Bottom_profile=31.33 mm; D1=92 mm; DN=125.3 mm; FOD=125 mm; Fillet_Length=6 mm  [stored 0.019685 ft]; Flange_thickness=19 mm; H3=470 mm; ID=62.65 mm; L=400 mm; L1=417 mm; L_Ref=408.5 mm; PG_Dia=62.65 mm; PG_Ref=66.67 mm; PG_depth=8.4 mm  [stored 0.0275591 ft]; PG_ref=72.65 mm; Pilot_Dia_1=27.5 mm; Pilot_Dia_2=55 mm; Pilot_Dia_3=18.33 mm; Pilot_Dia_4=9.17 mm; Pilot_Dia_5=6.11 mm; Pilot_top_1=300 mm; Pilot_top_ref=45 mm; Profile1_Height=195 mm; Profile1_Length=33.78 mm; Profile1_Length_2=22.52 mm; Profile_Dia=6 mm  [stored 0.019685 ft]; Profile_Dia_2=6 mm  [stored 0.019685 ft]; Profile_Dia_3=12 mm  [stored 0.0393701 ft]; Top_Profile=160 mm; Top_Profile_Ref=165 mm; Top_Ref=255 mm; Top_Ref_2=277.5 mm; W=310 mm; W_Ref=307 mm
- 879-0125-00-14400229999_DN125_PN10/16: Body_Collar_Dia=41.67 mm; Body_Collar_Dia_2=35.87 mm; Body_Flange_Dia=129.03 mm; Body_Flange_Dia_2=142.86 mm; Body_Height_1=100 mm; Body_Height_2=50 mm; Body_Height_3=58.5 mm; Body_Height_4=65 mm; Body_Top_Dia=17.94 mm; Body_Top_Dia_2=14.95 mm; Body_With_Dia=100 mm; Body_With_Dia_2=108.11 mm; Bolt_support=266.67 mm; Bolt_support_2=133.33 mm; Bolt_support_Dia=12 mm  [stored 0.0393701 ft]; Bolt_support_lenght=82.7 mm; Bolt_support_lenght_2=92.7 mm; Bottom_profile=31.35 mm; D1=92 mm; DN=125.4 mm; FOD=125 mm; Fillet_Length=6 mm  [stored 0.019685 ft]; Flange_thickness=19 mm; H3=470 mm; ID=62.7 mm; L=400 mm; L1=417 mm; L_Ref=408.5 mm; PG_Dia=62.7 mm; PG_Ref=66.67 mm; PG_depth=8.4 mm  [stored 0.0275591 ft]; PG_ref=72.7 mm; Pilot_Dia_1=27.5 mm; Pilot_Dia_2=55 mm; Pilot_Dia_3=18.33 mm; Pilot_Dia_4=9.17 mm; Pilot_Dia_5=6.11 mm; Pilot_top_1=294.25 mm; Pilot_top_ref=50.75 mm; Profile1_Height=205 mm; Profile1_Length=33.78 mm; Profile1_Length_2=22.52 mm; Profile_Dia=6 mm  [stored 0.019685 ft]; Profile_Dia_2=6 mm  [stored 0.019685 ft]; Profile_Dia_3=12 mm  [stored 0.0393701 ft]; Top_Profile=160 mm; Top_Profile_Ref=165 mm; Top_Ref=243.5 mm; Top_Ref_2=268.88 mm; W=310 mm; W_Ref=307 mm
- 879-0125-00-144002299A0_DN125_PN10/16: Body_Collar_Dia=41.67 mm; Body_Collar_Dia_2=35.87 mm; Body_Flange_Dia=129.03 mm; Body_Flange_Dia_2=142.86 mm; Body_Height_1=100 mm; Body_Height_2=50 mm; Body_Height_3=70 mm; Body_Height_4=65 mm; Body_Top_Dia=17.94 mm; Body_Top_Dia_2=14.95 mm; Body_With_Dia=100 mm; Body_With_Dia_2=108.11 mm; Bolt_support=266.67 mm; Bolt_support_2=133.33 mm; Bolt_support_Dia=12 mm  [stored 0.0393701 ft]; Bolt_support_lenght=82.75 mm; Bolt_support_lenght_2=92.75 mm; Bottom_profile=31.38 mm; D1=92 mm; DN=125.5 mm; FOD=125 mm; Fillet_Length=6 mm  [stored 0.019685 ft]; Flange_thickness=19 mm; H3=470 mm; ID=62.75 mm; L=400 mm; L1=417 mm; L_Ref=408.5 mm; PG_Dia=62.75 mm; PG_Ref=66.67 mm; PG_depth=8.4 mm  [stored 0.0275591 ft]; PG_ref=72.75 mm; Pilot_Dia_1=27.5 mm; Pilot_Dia_2=55 mm; Pilot_Dia_3=18.33 mm; Pilot_Dia_4=9.17 mm; Pilot_Dia_5=6.11 mm; Pilot_top_1=300 mm; Pilot_top_ref=45 mm; Profile1_Height=195 mm; Profile1_Length=33.78 mm; Profile1_Length_2=22.52 mm; Profile_Dia=6 mm  [stored 0.019685 ft]; Profile_Dia_2=6 mm  [stored 0.019685 ft]; Profile_Dia_3=12 mm  [stored 0.0393701 ft]; Top_Profile=160 mm; Top_Profile_Ref=165 mm; Top_Ref=255 mm; Top_Ref_2=277.5 mm; W=310 mm; W_Ref=307 mm
- 879-0150-00-14400209999_DN150_PN10/16: Body_Collar_Dia=50 mm; Body_Collar_Dia_2=43.05 mm; Body_Flange_Dia=154.84 mm; Body_Flange_Dia_2=171.43 mm; Body_Height_1=120 mm; Body_Height_2=60 mm; Body_Height_3=60 mm; Body_Height_4=75 mm; Body_Top_Dia=21.52 mm; Body_Top_Dia_2=17.94 mm; Body_With_Dia=120 mm; Body_With_Dia_2=129.73 mm; Bolt_support=320 mm; Bolt_support_2=160 mm; Bolt_support_Dia=16 mm  [stored 0.0524934 ft]; Bolt_support_lenght=95 mm; Bolt_support_lenght_2=105 mm; Bottom_profile=37.5 mm; D1=105.5 mm; DN=150 mm; FOD=142.5 mm; Fillet_Length=8 mm  [stored 0.0262467 ft]; Flange_thickness=19 mm; H3=495 mm; ID=75 mm; L=480 mm; L1=497 mm; L_Ref=488.5 mm; PG_Dia=50 mm; PG_Ref=80 mm; PG_depth=11.2 mm  [stored 0.0367454 ft]; PG_ref=85 mm; Pilot_Dia_1=31 mm; Pilot_Dia_2=62 mm; Pilot_Dia_3=20.67 mm; Pilot_Dia_4=10.33 mm; Pilot_Dia_5=6.89 mm; Pilot_top_1=313.75 mm; Pilot_top_ref=38.75 mm; Profile1_Height=230 mm; Profile1_Length=38.51 mm; Profile1_Length_2=25.68 mm; Profile_Dia=8 mm  [stored 0.0262467 ft]; Profile_Dia_2=8 mm  [stored 0.0262467 ft]; Profile_Dia_3=16 mm  [stored 0.0524934 ft]; Top_Profile=192 mm; Top_Profile_Ref=197 mm; Top_Ref=275 mm; Top_Ref_2=294.38 mm; W=340 mm; W_Ref=336 mm
- 879-0150-00-144002099A0_DN150_PN10/16: Body_Collar_Dia=50 mm; Body_Collar_Dia_2=43.05 mm; Body_Flange_Dia=154.84 mm; Body_Flange_Dia_2=171.43 mm; Body_Height_1=120 mm; Body_Height_2=60 mm; Body_Height_3=68 mm; Body_Height_4=75 mm; Body_Top_Dia=21.52 mm; Body_Top_Dia_2=17.94 mm; Body_With_Dia=120 mm; Body_With_Dia_2=129.73 mm; Bolt_support=320 mm; Bolt_support_2=160 mm; Bolt_support_Dia=16 mm  [stored 0.0524934 ft]; Bolt_support_lenght=95.05 mm; Bolt_support_lenght_2=105.05 mm; Bottom_profile=37.53 mm; D1=105.5 mm; DN=150.1 mm; FOD=142.5 mm; Fillet_Length=8 mm  [stored 0.0262467 ft]; Flange_thickness=19 mm; H3=495 mm; ID=75.05 mm; L=480 mm; L1=497 mm; L_Ref=488.5 mm; PG_Dia=50.03 mm; PG_Ref=80 mm; PG_depth=11.2 mm  [stored 0.0367454 ft]; PG_ref=85.05 mm; Pilot_Dia_1=31 mm; Pilot_Dia_2=62 mm; Pilot_Dia_3=20.67 mm; Pilot_Dia_4=10.33 mm; Pilot_Dia_5=6.89 mm; Pilot_top_1=317.75 mm; Pilot_top_ref=34.75 mm; Profile1_Height=230 mm; Profile1_Length=38.51 mm; Profile1_Length_2=25.68 mm; Profile_Dia=8 mm  [stored 0.0262467 ft]; Profile_Dia_2=8 mm  [stored 0.0262467 ft]; Profile_Dia_3=16 mm  [stored 0.0524934 ft]; Top_Profile=192 mm; Top_Profile_Ref=197 mm; Top_Ref=283 mm; Top_Ref_2=300.38 mm; W=340 mm; W_Ref=336 mm
- 879-0150-00-14400219999_DN150_PN10/16: Body_Collar_Dia=50 mm; Body_Collar_Dia_2=43.05 mm; Body_Flange_Dia=154.84 mm; Body_Flange_Dia_2=171.43 mm; Body_Height_1=120 mm; Body_Height_2=60 mm; Body_Height_3=60 mm; Body_Height_4=75 mm; Body_Top_Dia=21.52 mm; Body_Top_Dia_2=17.94 mm; Body_With_Dia=120 mm; Body_With_Dia_2=129.73 mm; Bolt_support=320 mm; Bolt_support_2=160 mm; Bolt_support_Dia=16 mm  [stored 0.0524934 ft]; Bolt_support_lenght=95.1 mm; Bolt_support_lenght_2=105.1 mm; Bottom_profile=37.55 mm; D1=105.5 mm; DN=150.2 mm; FOD=142.5 mm; Fillet_Length=8 mm  [stored 0.0262467 ft]; Flange_thickness=19 mm; H3=495 mm; ID=75.1 mm; L=480 mm; L1=497 mm; L_Ref=488.5 mm; PG_Dia=50.07 mm; PG_Ref=80 mm; PG_depth=11.2 mm  [stored 0.0367454 ft]; PG_ref=85.1 mm; Pilot_Dia_1=31 mm; Pilot_Dia_2=62 mm; Pilot_Dia_3=20.67 mm; Pilot_Dia_4=10.33 mm; Pilot_Dia_5=6.89 mm; Pilot_top_1=313.75 mm; Pilot_top_ref=38.75 mm; Profile1_Height=230 mm; Profile1_Length=38.51 mm; Profile1_Length_2=25.68 mm; Profile_Dia=8 mm  [stored 0.0262467 ft]; Profile_Dia_2=8 mm  [stored 0.0262467 ft]; Profile_Dia_3=16 mm  [stored 0.0524934 ft]; Top_Profile=192 mm; Top_Profile_Ref=197 mm; Top_Ref=275 mm; Top_Ref_2=294.38 mm; W=340 mm; W_Ref=336 mm
- 879-0150-00-144002199A0_DN150_PN10/16: Body_Collar_Dia=50 mm; Body_Collar_Dia_2=43.05 mm; Body_Flange_Dia=154.84 mm; Body_Flange_Dia_2=171.43 mm; Body_Height_1=120 mm; Body_Height_2=60 mm; Body_Height_3=68 mm; Body_Height_4=75 mm; Body_Top_Dia=21.52 mm; Body_Top_Dia_2=17.94 mm; Body_With_Dia=120 mm; Body_With_Dia_2=129.73 mm; Bolt_support=320 mm; Bolt_support_2=160 mm; Bolt_support_Dia=16 mm  [stored 0.0524934 ft]; Bolt_support_lenght=95.15 mm; Bolt_support_lenght_2=105.15 mm; Bottom_profile=37.58 mm; D1=105.5 mm; DN=150.3 mm; FOD=142.5 mm; Fillet_Length=8 mm  [stored 0.0262467 ft]; Flange_thickness=19 mm; H3=495 mm; ID=75.15 mm; L=480 mm; L1=497 mm; L_Ref=488.5 mm; PG_Dia=50.1 mm; PG_Ref=80 mm; PG_depth=11.2 mm  [stored 0.0367454 ft]; PG_ref=85.15 mm; Pilot_Dia_1=31 mm; Pilot_Dia_2=62 mm; Pilot_Dia_3=20.67 mm; Pilot_Dia_4=10.33 mm; Pilot_Dia_5=6.89 mm; Pilot_top_1=317.75 mm; Pilot_top_ref=34.75 mm; Profile1_Height=230 mm; Profile1_Length=38.51 mm; Profile1_Length_2=25.68 mm; Profile_Dia=8 mm  [stored 0.0262467 ft]; Profile_Dia_2=8 mm  [stored 0.0262467 ft]; Profile_Dia_3=16 mm  [stored 0.0524934 ft]; Top_Profile=192 mm; Top_Profile_Ref=197 mm; Top_Ref=283 mm; Top_Ref_2=300.38 mm; W=340 mm; W_Ref=336 mm
- 879-0150-00-14400229999_DN150_PN10/16: Body_Collar_Dia=50 mm; Body_Collar_Dia_2=43.05 mm; Body_Flange_Dia=154.84 mm; Body_Flange_Dia_2=171.43 mm; Body_Height_1=120 mm; Body_Height_2=60 mm; Body_Height_3=60 mm; Body_Height_4=75 mm; Body_Top_Dia=21.52 mm; Body_Top_Dia_2=17.94 mm; Body_With_Dia=120 mm; Body_With_Dia_2=129.73 mm; Bolt_support=320 mm; Bolt_support_2=160 mm; Bolt_support_Dia=16 mm  [stored 0.0524934 ft]; Bolt_support_lenght=95.2 mm; Bolt_support_lenght_2=105.2 mm; Bottom_profile=37.6 mm; D1=105.5 mm; DN=150.4 mm; FOD=142.5 mm; Fillet_Length=8 mm  [stored 0.0262467 ft]; Flange_thickness=19 mm; H3=495 mm; ID=75.2 mm; L=480 mm; L1=497 mm; L_Ref=488.5 mm; PG_Dia=50.13 mm; PG_Ref=80 mm; PG_depth=11.2 mm  [stored 0.0367454 ft]; PG_ref=85.2 mm; Pilot_Dia_1=31 mm; Pilot_Dia_2=62 mm; Pilot_Dia_3=20.67 mm; Pilot_Dia_4=10.33 mm; Pilot_Dia_5=6.89 mm; Pilot_top_1=313.75 mm; Pilot_top_ref=38.75 mm; Profile1_Height=230 mm; Profile1_Length=38.51 mm; Profile1_Length_2=25.68 mm; Profile_Dia=8 mm  [stored 0.0262467 ft]; Profile_Dia_2=8 mm  [stored 0.0262467 ft]; Profile_Dia_3=16 mm  [stored 0.0524934 ft]; Top_Profile=192 mm; Top_Profile_Ref=197 mm; Top_Ref=275 mm; Top_Ref_2=294.38 mm; W=340 mm; W_Ref=336 mm
- 879-0150-00-144002299A0_DN150_PN10/16: Body_Collar_Dia=50 mm; Body_Collar_Dia_2=43.05 mm; Body_Flange_Dia=154.84 mm; Body_Flange_Dia_2=171.43 mm; Body_Height_1=120 mm; Body_Height_2=60 mm; Body_Height_3=68 mm; Body_Height_4=75 mm; Body_Top_Dia=21.52 mm; Body_Top_Dia_2=17.94 mm; Body_With_Dia=120 mm; Body_With_Dia_2=129.73 mm; Bolt_support=320 mm; Bolt_support_2=160 mm; Bolt_support_Dia=16 mm  [stored 0.0524934 ft]; Bolt_support_lenght=95.25 mm; Bolt_support_lenght_2=105.25 mm; Bottom_profile=37.63 mm; D1=105.5 mm; DN=150.5 mm; FOD=142.5 mm; Fillet_Length=8 mm  [stored 0.0262467 ft]; Flange_thickness=19 mm; H3=495 mm; ID=75.25 mm; L=480 mm; L1=497 mm; L_Ref=488.5 mm; PG_Dia=50.17 mm; PG_Ref=80 mm; PG_depth=11.2 mm  [stored 0.0367454 ft]; PG_ref=85.25 mm; Pilot_Dia_1=31 mm; Pilot_Dia_2=62 mm; Pilot_Dia_3=20.67 mm; Pilot_Dia_4=10.33 mm; Pilot_Dia_5=6.89 mm; Pilot_top_1=317.75 mm; Pilot_top_ref=34.75 mm; Profile1_Height=230 mm; Profile1_Length=38.51 mm; Profile1_Length_2=25.68 mm; Profile_Dia=8 mm  [stored 0.0262467 ft]; Profile_Dia_2=8 mm  [stored 0.0262467 ft]; Profile_Dia_3=16 mm  [stored 0.0524934 ft]; Top_Profile=192 mm; Top_Profile_Ref=197 mm; Top_Ref=283 mm; Top_Ref_2=300.38 mm; W=340 mm; W_Ref=336 mm
- 879-0150-00-14400239999_DN150_PN10/16: Body_Collar_Dia=50 mm; Body_Collar_Dia_2=43.05 mm; Body_Flange_Dia=154.84 mm; Body_Flange_Dia_2=171.43 mm; Body_Height_1=120 mm; Body_Height_2=60 mm; Body_Height_3=60 mm; Body_Height_4=75 mm; Body_Top_Dia=21.52 mm; Body_Top_Dia_2=17.94 mm; Body_With_Dia=120 mm; Body_With_Dia_2=129.73 mm; Bolt_support=320 mm; Bolt_support_2=160 mm; Bolt_support_Dia=16 mm  [stored 0.0524934 ft]; Bolt_support_lenght=95.3 mm; Bolt_support_lenght_2=105.3 mm; Bottom_profile=37.65 mm; D1=105.5 mm; DN=150.6 mm; FOD=142.5 mm; Fillet_Length=8 mm  [stored 0.0262467 ft]; Flange_thickness=19 mm; H3=495 mm; ID=75.3 mm; L=480 mm; L1=497 mm; L_Ref=488.5 mm; PG_Dia=50.2 mm; PG_Ref=80 mm; PG_depth=11.2 mm  [stored 0.0367454 ft]; PG_ref=85.3 mm; Pilot_Dia_1=31 mm; Pilot_Dia_2=62 mm; Pilot_Dia_3=20.67 mm; Pilot_Dia_4=10.33 mm; Pilot_Dia_5=6.89 mm; Pilot_top_1=313.75 mm; Pilot_top_ref=38.75 mm; Profile1_Height=230 mm; Profile1_Length=38.51 mm; Profile1_Length_2=25.68 mm; Profile_Dia=8 mm  [stored 0.0262467 ft]; Profile_Dia_2=8 mm  [stored 0.0262467 ft]; Profile_Dia_3=16 mm  [stored 0.0524934 ft]; Top_Profile=192 mm; Top_Profile_Ref=197 mm; Top_Ref=275 mm; Top_Ref_2=294.38 mm; W=340 mm; W_Ref=336 mm
- 879-0150-00-144002399A0_DN150_PN10/16: Body_Collar_Dia=50 mm; Body_Collar_Dia_2=43.05 mm; Body_Flange_Dia=154.84 mm; Body_Flange_Dia_2=171.43 mm; Body_Height_1=120 mm; Body_Height_2=60 mm; Body_Height_3=68 mm; Body_Height_4=75 mm; Body_Top_Dia=21.52 mm; Body_Top_Dia_2=17.94 mm; Body_With_Dia=120 mm; Body_With_Dia_2=129.73 mm; Bolt_support=320 mm; Bolt_support_2=160 mm; Bolt_support_Dia=16 mm  [stored 0.0524934 ft]; Bolt_support_lenght=95.35 mm; Bolt_support_lenght_2=105.35 mm; Bottom_profile=37.68 mm; D1=105.5 mm; DN=150.7 mm; FOD=142.5 mm; Fillet_Length=8 mm  [stored 0.0262467 ft]; Flange_thickness=19 mm; H3=495 mm; ID=75.35 mm; L=480 mm; L1=497 mm; L_Ref=488.5 mm; PG_Dia=50.23 mm; PG_Ref=80 mm; PG_depth=11.2 mm  [stored 0.0367454 ft]; PG_ref=85.35 mm; Pilot_Dia_1=31 mm; Pilot_Dia_2=62 mm; Pilot_Dia_3=20.67 mm; Pilot_Dia_4=10.33 mm; Pilot_Dia_5=6.89 mm; Pilot_top_1=317.75 mm; Pilot_top_ref=34.75 mm; Profile1_Height=230 mm; Profile1_Length=38.51 mm; Profile1_Length_2=25.68 mm; Profile_Dia=8 mm  [stored 0.0262467 ft]; Profile_Dia_2=8 mm  [stored 0.0262467 ft]; Profile_Dia_3=16 mm  [stored 0.0524934 ft]; Top_Profile=192 mm; Top_Profile_Ref=197 mm; Top_Ref=283 mm; Top_Ref_2=300.38 mm; W=340 mm; W_Ref=336 mm
- 879-0200-00-14400209999_DN200_PN16: Body_Collar_Dia=62.5 mm; Body_Collar_Dia_2=53.81 mm; Body_Flange_Dia=193.55 mm; Body_Flange_Dia_2=214.29 mm; Body_Height_1=150 mm; Body_Height_2=75 mm; Body_Height_3=75 mm; Body_Height_4=90 mm; Body_Top_Dia=26.91 mm; Body_Top_Dia_2=22.42 mm; Body_With_Dia=150 mm; Body_With_Dia_2=162.16 mm; Bolt_support=400 mm; Bolt_support_2=200 mm; Bolt_support_Dia=20 mm; Bolt_support_lenght=120 mm; Bolt_support_lenght_2=130 mm; Bottom_profile=50 mm; D1=133 mm; DN=200 mm; FOD=170 mm; Fillet_Length=10 mm  [stored 0.0328084 ft]; Flange_thickness=20 mm; H3=585 mm; ID=100 mm; L=600 mm; L1=617 mm; L_Ref=608.5 mm; PG_Dia=66.67 mm; PG_Ref=100 mm; PG_depth=14 mm  [stored 0.0459318 ft]; PG_ref=110 mm; Pilot_Dia_1=38.5 mm; Pilot_Dia_2=77 mm; Pilot_Dia_3=25.67 mm; Pilot_Dia_4=12.83 mm; Pilot_Dia_5=8.56 mm; Pilot_top_1=375 mm; Pilot_top_ref=40 mm; Profile1_Height=273 mm; Profile1_Length=45.95 mm; Profile1_Length_2=30.63 mm; Profile_Dia=10 mm  [stored 0.0328084 ft]; Profile_Dia_2=10 mm  [stored 0.0328084 ft]; Profile_Dia_3=20 mm; Top_Profile=240 mm; Top_Profile_Ref=245 mm; Top_Ref=335 mm; Top_Ref_2=355 mm; W=425 mm; W_Ref=420 mm
- 879-0200-00-144002099A0_DN200_PN16: Body_Collar_Dia=62.5 mm; Body_Collar_Dia_2=53.81 mm; Body_Flange_Dia=193.55 mm; Body_Flange_Dia_2=214.29 mm; Body_Height_1=150 mm; Body_Height_2=75 mm; Body_Height_3=100 mm; Body_Height_4=90 mm; Body_Top_Dia=26.91 mm; Body_Top_Dia_2=22.42 mm; Body_With_Dia=150 mm; Body_With_Dia_2=162.16 mm; Bolt_support=400 mm; Bolt_support_2=200 mm; Bolt_support_Dia=20 mm; Bolt_support_lenght=120.05 mm; Bolt_support_lenght_2=130.05 mm; Bottom_profile=50.03 mm; D1=133 mm; DN=200.1 mm; FOD=170 mm; Fillet_Length=10 mm  [stored 0.0328084 ft]; Flange_thickness=20 mm; H3=585 mm; ID=100.05 mm; L=600 mm; L1=617 mm; L_Ref=608.5 mm; PG_Dia=66.7 mm; PG_Ref=100 mm; PG_depth=14 mm  [stored 0.0459318 ft]; PG_ref=110.05 mm; Pilot_Dia_1=38.5 mm; Pilot_Dia_2=77 mm; Pilot_Dia_3=25.67 mm; Pilot_Dia_4=12.83 mm; Pilot_Dia_5=8.56 mm; Pilot_top_1=387.5 mm; Pilot_top_ref=27.5 mm; Profile1_Height=275 mm; Profile1_Length=45.95 mm; Profile1_Length_2=30.63 mm; Profile_Dia=10 mm  [stored 0.0328084 ft]; Profile_Dia_2=10 mm  [stored 0.0328084 ft]; Profile_Dia_3=20 mm; Top_Profile=240 mm; Top_Profile_Ref=245 mm; Top_Ref=360 mm; Top_Ref_2=373.75 mm; W=425 mm; W_Ref=420 mm
- 879-0200-00-14400219999_DN200_PN16: Body_Collar_Dia=62.5 mm; Body_Collar_Dia_2=53.81 mm; Body_Flange_Dia=193.55 mm; Body_Flange_Dia_2=214.29 mm; Body_Height_1=150 mm; Body_Height_2=75 mm; Body_Height_3=75 mm; Body_Height_4=90 mm; Body_Top_Dia=26.91 mm; Body_Top_Dia_2=22.42 mm; Body_With_Dia=150 mm; Body_With_Dia_2=162.16 mm; Bolt_support=400 mm; Bolt_support_2=200 mm; Bolt_support_Dia=20 mm; Bolt_support_lenght=120.1 mm; Bolt_support_lenght_2=130.1 mm; Bottom_profile=50.05 mm; D1=133 mm; DN=200.2 mm; FOD=170 mm; Fillet_Length=10 mm  [stored 0.0328084 ft]; Flange_thickness=20 mm; H3=585 mm; ID=100.1 mm; L=600 mm; L1=617 mm; L_Ref=608.5 mm; PG_Dia=66.73 mm; PG_Ref=100 mm; PG_depth=14 mm  [stored 0.0459318 ft]; PG_ref=110.1 mm; Pilot_Dia_1=38.5 mm; Pilot_Dia_2=77 mm; Pilot_Dia_3=25.67 mm; Pilot_Dia_4=12.83 mm; Pilot_Dia_5=8.56 mm; Pilot_top_1=375 mm; Pilot_top_ref=40 mm; Profile1_Height=273 mm; Profile1_Length=45.95 mm; Profile1_Length_2=30.63 mm; Profile_Dia=10 mm  [stored 0.0328084 ft]; Profile_Dia_2=10 mm  [stored 0.0328084 ft]; Profile_Dia_3=20 mm; Top_Profile=240 mm; Top_Profile_Ref=245 mm; Top_Ref=335 mm; Top_Ref_2=355 mm; W=425 mm; W_Ref=420 mm
- 879-0200-00-144002199A0_DN200_PN16: Body_Collar_Dia=62.5 mm; Body_Collar_Dia_2=53.81 mm; Body_Flange_Dia=193.55 mm; Body_Flange_Dia_2=214.29 mm; Body_Height_1=150 mm; Body_Height_2=75 mm; Body_Height_3=86 mm; Body_Height_4=90 mm; Body_Top_Dia=26.91 mm; Body_Top_Dia_2=22.42 mm; Body_With_Dia=150 mm; Body_With_Dia_2=162.16 mm; Bolt_support=400 mm; Bolt_support_2=200 mm; Bolt_support_Dia=20 mm; Bolt_support_lenght=120.15 mm; Bolt_support_lenght_2=130.15 mm; Bottom_profile=50.08 mm; D1=133 mm; DN=200.3 mm; FOD=170 mm; Fillet_Length=10 mm  [stored 0.0328084 ft]; Flange_thickness=20 mm; H3=585 mm; ID=100.15 mm; L=600 mm; L1=617 mm; L_Ref=608.5 mm; PG_Dia=66.77 mm; PG_Ref=100 mm; PG_depth=14 mm  [stored 0.0459318 ft]; PG_ref=110.15 mm; Pilot_Dia_1=38.5 mm; Pilot_Dia_2=77 mm; Pilot_Dia_3=25.67 mm; Pilot_Dia_4=12.83 mm; Pilot_Dia_5=8.56 mm; Pilot_top_1=380.5 mm; Pilot_top_ref=34.5 mm; Profile1_Height=275 mm; Profile1_Length=45.95 mm; Profile1_Length_2=30.63 mm; Profile_Dia=10 mm  [stored 0.0328084 ft]; Profile_Dia_2=10 mm  [stored 0.0328084 ft]; Profile_Dia_3=20 mm; Top_Profile=240 mm; Top_Profile_Ref=245 mm; Top_Ref=346 mm; Top_Ref_2=363.25 mm; W=425 mm; W_Ref=420 mm
- 879-0200-00-14400229999_DN200_PN16: Body_Collar_Dia=62.5 mm; Body_Collar_Dia_2=53.81 mm; Body_Flange_Dia=193.55 mm; Body_Flange_Dia_2=214.29 mm; Body_Height_1=150 mm; Body_Height_2=75 mm; Body_Height_3=75 mm; Body_Height_4=90 mm; Body_Top_Dia=26.91 mm; Body_Top_Dia_2=22.42 mm; Body_With_Dia=150 mm; Body_With_Dia_2=162.16 mm; Bolt_support=400 mm; Bolt_support_2=200 mm; Bolt_support_Dia=20 mm; Bolt_support_lenght=120.2 mm; Bolt_support_lenght_2=130.2 mm; Bottom_profile=50.1 mm; D1=133 mm; DN=200.4 mm; FOD=170 mm; Fillet_Length=10 mm  [stored 0.0328084 ft]; Flange_thickness=20 mm; H3=585 mm; ID=100.2 mm; L=600 mm; L1=617 mm; L_Ref=608.5 mm; PG_Dia=66.8 mm; PG_Ref=100 mm; PG_depth=14 mm  [stored 0.0459318 ft]; PG_ref=110.2 mm; Pilot_Dia_1=38.5 mm; Pilot_Dia_2=77 mm; Pilot_Dia_3=25.67 mm; Pilot_Dia_4=12.83 mm; Pilot_Dia_5=8.56 mm; Pilot_top_1=375 mm; Pilot_top_ref=40 mm; Profile1_Height=273 mm; Profile1_Length=45.95 mm; Profile1_Length_2=30.63 mm; Profile_Dia=10 mm  [stored 0.0328084 ft]; Profile_Dia_2=10 mm  [stored 0.0328084 ft]; Profile_Dia_3=20 mm; Top_Profile=240 mm; Top_Profile_Ref=245 mm; Top_Ref=335 mm; Top_Ref_2=355 mm; W=425 mm; W_Ref=420 mm
- 879-0200-00-144002299A0_DN200_PN16: Body_Collar_Dia=62.5 mm; Body_Collar_Dia_2=53.81 mm; Body_Flange_Dia=193.55 mm; Body_Flange_Dia_2=214.29 mm; Body_Height_1=150 mm; Body_Height_2=75 mm; Body_Height_3=100 mm; Body_Height_4=90 mm; Body_Top_Dia=26.91 mm; Body_Top_Dia_2=22.42 mm; Body_With_Dia=150 mm; Body_With_Dia_2=162.16 mm; Bolt_support=400 mm; Bolt_support_2=200 mm; Bolt_support_Dia=20 mm; Bolt_support_lenght=120.25 mm; Bolt_support_lenght_2=130.25 mm; Bottom_profile=50.13 mm; D1=133 mm; DN=200.5 mm; FOD=170 mm; Fillet_Length=10 mm  [stored 0.0328084 ft]; Flange_thickness=20 mm; H3=585 mm; ID=100.25 mm; L=600 mm; L1=617 mm; L_Ref=608.5 mm; PG_Dia=66.83 mm; PG_Ref=100 mm; PG_depth=14 mm  [stored 0.0459318 ft]; PG_ref=110.25 mm; Pilot_Dia_1=38.5 mm; Pilot_Dia_2=77 mm; Pilot_Dia_3=25.67 mm; Pilot_Dia_4=12.83 mm; Pilot_Dia_5=8.56 mm; Pilot_top_1=387.5 mm; Pilot_top_ref=27.5 mm; Profile1_Height=275 mm; Profile1_Length=45.95 mm; Profile1_Length_2=30.63 mm; Profile_Dia=10 mm  [stored 0.0328084 ft]; Profile_Dia_2=10 mm  [stored 0.0328084 ft]; Profile_Dia_3=20 mm; Top_Profile=240 mm; Top_Profile_Ref=245 mm; Top_Ref=360 mm; Top_Ref_2=373.75 mm; W=425 mm; W_Ref=420 mm
- 879-0200-00-14400239999_DN200_PN16: Body_Collar_Dia=62.5 mm; Body_Collar_Dia_2=53.81 mm; Body_Flange_Dia=193.55 mm; Body_Flange_Dia_2=214.29 mm; Body_Height_1=150 mm; Body_Height_2=75 mm; Body_Height_3=75 mm; Body_Height_4=90 mm; Body_Top_Dia=26.91 mm; Body_Top_Dia_2=22.42 mm; Body_With_Dia=150 mm; Body_With_Dia_2=162.16 mm; Bolt_support=400 mm; Bolt_support_2=200 mm; Bolt_support_Dia=20 mm; Bolt_support_lenght=120.3 mm; Bolt_support_lenght_2=130.3 mm; Bottom_profile=50.15 mm; D1=133 mm; DN=200.6 mm; FOD=170 mm; Fillet_Length=10 mm  [stored 0.0328084 ft]; Flange_thickness=20 mm; H3=585 mm; ID=100.3 mm; L=600 mm; L1=617 mm; L_Ref=608.5 mm; PG_Dia=66.87 mm; PG_Ref=100 mm; PG_depth=14 mm  [stored 0.0459318 ft]; PG_ref=110.3 mm; Pilot_Dia_1=38.5 mm; Pilot_Dia_2=77 mm; Pilot_Dia_3=25.67 mm; Pilot_Dia_4=12.83 mm; Pilot_Dia_5=8.56 mm; Pilot_top_1=375 mm; Pilot_top_ref=40 mm; Profile1_Height=273 mm; Profile1_Length=45.95 mm; Profile1_Length_2=30.63 mm; Profile_Dia=10 mm  [stored 0.0328084 ft]; Profile_Dia_2=10 mm  [stored 0.0328084 ft]; Profile_Dia_3=20 mm; Top_Profile=240 mm; Top_Profile_Ref=245 mm; Top_Ref=335 mm; Top_Ref_2=355 mm; W=425 mm; W_Ref=420 mm
- 879-0200-00-144002399A0_DN200_PN16: Body_Collar_Dia=62.5 mm; Body_Collar_Dia_2=53.81 mm; Body_Flange_Dia=193.55 mm; Body_Flange_Dia_2=214.29 mm; Body_Height_1=150 mm; Body_Height_2=75 mm; Body_Height_3=86 mm; Body_Height_4=90 mm; Body_Top_Dia=26.91 mm; Body_Top_Dia_2=22.42 mm; Body_With_Dia=150 mm; Body_With_Dia_2=162.16 mm; Bolt_support=400 mm; Bolt_support_2=200 mm; Bolt_support_Dia=20 mm; Bolt_support_lenght=120.35 mm; Bolt_support_lenght_2=130.35 mm; Bottom_profile=50.18 mm; D1=133 mm; DN=200.7 mm; FOD=170 mm; Fillet_Length=10 mm  [stored 0.0328084 ft]; Flange_thickness=20 mm; H3=585 mm; ID=100.35 mm; L=600 mm; L1=617 mm; L_Ref=608.5 mm; PG_Dia=66.9 mm; PG_Ref=100 mm; PG_depth=14 mm  [stored 0.0459318 ft]; PG_ref=110.35 mm; Pilot_Dia_1=38.5 mm; Pilot_Dia_2=77 mm; Pilot_Dia_3=25.67 mm; Pilot_Dia_4=12.83 mm; Pilot_Dia_5=8.56 mm; Pilot_top_1=380.5 mm; Pilot_top_ref=34.5 mm; Profile1_Height=275 mm; Profile1_Length=45.95 mm; Profile1_Length_2=30.63 mm; Profile_Dia=10 mm  [stored 0.0328084 ft]; Profile_Dia_2=10 mm  [stored 0.0328084 ft]; Profile_Dia_3=20 mm; Top_Profile=240 mm; Top_Profile_Ref=245 mm; Top_Ref=346 mm; Top_Ref_2=363.25 mm; W=425 mm; W_Ref=420 mm
- 879-0250-00-14400209999_DN250_PN16: Body_Collar_Dia=76.04 mm; Body_Collar_Dia_2=65.47 mm; Body_Flange_Dia=235.48 mm; Body_Flange_Dia_2=260.71 mm; Body_Height_1=182.5 mm; Body_Height_2=91.25 mm; Body_Height_3=81 mm; Body_Height_4=106.25 mm; Body_Top_Dia=32.74 mm; Body_Top_Dia_2=27.28 mm; Body_With_Dia=182.5 mm; Body_With_Dia_2=197.3 mm; Bolt_support=486.67 mm; Bolt_support_2=243.33 mm; Bolt_support_Dia=20 mm; Bolt_support_lenght=145 mm; Bolt_support_lenght_2=155 mm; Bottom_profile=62.5 mm; D1=159.5 mm; DN=250 mm; FOD=202.5 mm; Fillet_Length=10 mm  [stored 0.0328084 ft]; Flange_thickness=22 mm; H3=690 mm; ID=125 mm; L=730 mm; L1=747 mm; L_Ref=738.5 mm; PG_Dia=83.33 mm; PG_Ref=121.67 mm; PG_depth=14 mm  [stored 0.0459318 ft]; PG_ref=135 mm; Pilot_Dia_1=46 mm; Pilot_Dia_2=92 mm; Pilot_Dia_3=30.67 mm; Pilot_Dia_4=15.33 mm; Pilot_Dia_5=10.22 mm; Pilot_top_1=438.63 mm; Pilot_top_ref=48.88 mm; Profile1_Height=327 mm; Profile1_Length=54.73 mm; Profile1_Length_2=36.49 mm; Profile_Dia=10 mm  [stored 0.0328084 ft]; Profile_Dia_2=10 mm  [stored 0.0328084 ft]; Profile_Dia_3=20 mm; Top_Profile=292 mm; Top_Profile_Ref=297 mm; Top_Ref=389.75 mm; Top_Ref_2=414.19 mm; W=510 mm; W_Ref=505 mm
- 879-0250-00-144002099A0_DN250_PN16: Body_Collar_Dia=76.04 mm; Body_Collar_Dia_2=65.47 mm; Body_Flange_Dia=235.48 mm; Body_Flange_Dia_2=260.71 mm; Body_Height_1=182.5 mm; Body_Height_2=91.25 mm; Body_Height_3=104.5 mm; Body_Height_4=106.25 mm; Body_Top_Dia=32.74 mm; Body_Top_Dia_2=27.28 mm; Body_With_Dia=182.5 mm; Body_With_Dia_2=197.3 mm; Bolt_support=486.67 mm; Bolt_support_2=243.33 mm; Bolt_support_Dia=20 mm; Bolt_support_lenght=145.05 mm; Bolt_support_lenght_2=155.05 mm; Bottom_profile=62.53 mm; D1=159.5 mm; DN=250.1 mm; FOD=202.5 mm; Fillet_Length=10 mm  [stored 0.0328084 ft]; Flange_thickness=22 mm; H3=690 mm; ID=125.05 mm; L=730 mm; L1=747 mm; L_Ref=738.5 mm; PG_Dia=83.37 mm; PG_Ref=121.67 mm; PG_depth=14 mm  [stored 0.0459318 ft]; PG_ref=135.05 mm; Pilot_Dia_1=46 mm; Pilot_Dia_2=92 mm; Pilot_Dia_3=30.67 mm; Pilot_Dia_4=15.33 mm; Pilot_Dia_5=10.22 mm; Pilot_top_1=450.38 mm; Pilot_top_ref=37.13 mm; Profile1_Height=330 mm; Profile1_Length=54.73 mm; Profile1_Length_2=36.49 mm; Profile_Dia=10 mm  [stored 0.0328084 ft]; Profile_Dia_2=10 mm  [stored 0.0328084 ft]; Profile_Dia_3=20 mm; Top_Profile=292 mm; Top_Profile_Ref=297 mm; Top_Ref=413.25 mm; Top_Ref_2=431.81 mm; W=510 mm; W_Ref=505 mm
- 879-0250-00-14400219999_DN250_PN16: Body_Collar_Dia=76.04 mm; Body_Collar_Dia_2=65.47 mm; Body_Flange_Dia=235.48 mm; Body_Flange_Dia_2=260.71 mm; Body_Height_1=182.5 mm; Body_Height_2=91.25 mm; Body_Height_3=81 mm; Body_Height_4=106.25 mm; Body_Top_Dia=32.74 mm; Body_Top_Dia_2=27.28 mm; Body_With_Dia=182.5 mm; Body_With_Dia_2=197.3 mm; Bolt_support=486.67 mm; Bolt_support_2=243.33 mm; Bolt_support_Dia=20 mm; Bolt_support_lenght=145.1 mm; Bolt_support_lenght_2=155.1 mm; Bottom_profile=62.55 mm; D1=159.5 mm; DN=250.2 mm; FOD=202.5 mm; Fillet_Length=10 mm  [stored 0.0328084 ft]; Flange_thickness=22 mm; H3=690 mm; ID=125.1 mm; L=730 mm; L1=747 mm; L_Ref=738.5 mm; PG_Dia=83.4 mm; PG_Ref=121.67 mm; PG_depth=14 mm  [stored 0.0459318 ft]; PG_ref=135.1 mm; Pilot_Dia_1=47 mm; Pilot_Dia_2=94 mm; Pilot_Dia_3=31.33 mm; Pilot_Dia_4=15.67 mm; Pilot_Dia_5=10.44 mm; Pilot_top_1=438.63 mm; Pilot_top_ref=48.88 mm; Profile1_Height=335 mm; Profile1_Length=54.73 mm; Profile1_Length_2=36.49 mm; Profile_Dia=10 mm  [stored 0.0328084 ft]; Profile_Dia_2=10 mm  [stored 0.0328084 ft]; Profile_Dia_3=20 mm; Top_Profile=292 mm; Top_Profile_Ref=297 mm; Top_Ref=389.75 mm; Top_Ref_2=414.19 mm; W=510 mm; W_Ref=505 mm
- 879-0250-00-144002199A0_DN250_PN16: Body_Collar_Dia=76.04 mm; Body_Collar_Dia_2=65.47 mm; Body_Flange_Dia=235.48 mm; Body_Flange_Dia_2=260.71 mm; Body_Height_1=182.5 mm; Body_Height_2=91.25 mm; Body_Height_3=81 mm; Body_Height_4=106.25 mm; Body_Top_Dia=32.74 mm; Body_Top_Dia_2=27.28 mm; Body_With_Dia=182.5 mm; Body_With_Dia_2=197.3 mm; Bolt_support=486.67 mm; Bolt_support_2=243.33 mm; Bolt_support_Dia=20 mm; Bolt_support_lenght=145.15 mm; Bolt_support_lenght_2=155.15 mm; Bottom_profile=62.58 mm; D1=159.5 mm; DN=250.3 mm; FOD=202.5 mm; Fillet_Length=10 mm  [stored 0.0328084 ft]; Flange_thickness=22 mm; H3=690 mm; ID=125.15 mm; L=730 mm; L1=747 mm; L_Ref=738.5 mm; PG_Dia=83.43 mm; PG_Ref=121.67 mm; PG_depth=14 mm  [stored 0.0459318 ft]; PG_ref=135.15 mm; Pilot_Dia_1=47 mm; Pilot_Dia_2=94 mm; Pilot_Dia_3=31.33 mm; Pilot_Dia_4=15.67 mm; Pilot_Dia_5=10.44 mm; Pilot_top_1=438.63 mm; Pilot_top_ref=48.88 mm; Profile1_Height=350 mm; Profile1_Length=54.73 mm; Profile1_Length_2=36.49 mm; Profile_Dia=10 mm  [stored 0.0328084 ft]; Profile_Dia_2=10 mm  [stored 0.0328084 ft]; Profile_Dia_3=20 mm; Top_Profile=292 mm; Top_Profile_Ref=297 mm; Top_Ref=389.75 mm; Top_Ref_2=414.19 mm; W=510 mm; W_Ref=505 mm
- 879-0250-00-14400229999_DN250_PN16: Body_Collar_Dia=76.04 mm; Body_Collar_Dia_2=65.47 mm; Body_Flange_Dia=235.48 mm; Body_Flange_Dia_2=260.71 mm; Body_Height_1=182.5 mm; Body_Height_2=91.25 mm; Body_Height_3=81 mm; Body_Height_4=106.25 mm; Body_Top_Dia=32.74 mm; Body_Top_Dia_2=27.28 mm; Body_With_Dia=182.5 mm; Body_With_Dia_2=197.3 mm; Bolt_support=486.67 mm; Bolt_support_2=243.33 mm; Bolt_support_Dia=20 mm; Bolt_support_lenght=145.2 mm; Bolt_support_lenght_2=155.2 mm; Bottom_profile=62.6 mm; D1=159.5 mm; DN=250.4 mm; FOD=202.5 mm; Fillet_Length=10 mm  [stored 0.0328084 ft]; Flange_thickness=22 mm; H3=690 mm; ID=125.2 mm; L=730 mm; L1=747 mm; L_Ref=738.5 mm; PG_Dia=83.47 mm; PG_Ref=121.67 mm; PG_depth=14 mm  [stored 0.0459318 ft]; PG_ref=135.2 mm; Pilot_Dia_1=46 mm; Pilot_Dia_2=92 mm; Pilot_Dia_3=30.67 mm; Pilot_Dia_4=15.33 mm; Pilot_Dia_5=10.22 mm; Pilot_top_1=438.63 mm; Pilot_top_ref=48.88 mm; Profile1_Height=327 mm; Profile1_Length=54.73 mm; Profile1_Length_2=36.49 mm; Profile_Dia=10 mm  [stored 0.0328084 ft]; Profile_Dia_2=10 mm  [stored 0.0328084 ft]; Profile_Dia_3=20 mm; Top_Profile=292 mm; Top_Profile_Ref=297 mm; Top_Ref=389.75 mm; Top_Ref_2=414.19 mm; W=510 mm; W_Ref=505 mm
- 879-0250-00-144002299A0_DN250_PN16: Body_Collar_Dia=76.04 mm; Body_Collar_Dia_2=65.47 mm; Body_Flange_Dia=235.48 mm; Body_Flange_Dia_2=260.71 mm; Body_Height_1=182.5 mm; Body_Height_2=91.25 mm; Body_Height_3=104.5 mm; Body_Height_4=106.25 mm; Body_Top_Dia=32.74 mm; Body_Top_Dia_2=27.28 mm; Body_With_Dia=182.5 mm; Body_With_Dia_2=197.3 mm; Bolt_support=486.67 mm; Bolt_support_2=243.33 mm; Bolt_support_Dia=20 mm; Bolt_support_lenght=145.25 mm; Bolt_support_lenght_2=155.25 mm; Bottom_profile=62.63 mm; D1=159.5 mm; DN=250.5 mm; FOD=202.5 mm; Fillet_Length=10 mm  [stored 0.0328084 ft]; Flange_thickness=22 mm; H3=690 mm; ID=125.25 mm; L=730 mm; L1=747 mm; L_Ref=738.5 mm; PG_Dia=83.5 mm; PG_Ref=121.67 mm; PG_depth=14 mm  [stored 0.0459318 ft]; PG_ref=135.25 mm; Pilot_Dia_1=46 mm; Pilot_Dia_2=92 mm; Pilot_Dia_3=30.67 mm; Pilot_Dia_4=15.33 mm; Pilot_Dia_5=10.22 mm; Pilot_top_1=450.38 mm; Pilot_top_ref=37.13 mm; Profile1_Height=330 mm; Profile1_Length=54.73 mm; Profile1_Length_2=36.49 mm; Profile_Dia=10 mm  [stored 0.0328084 ft]; Profile_Dia_2=10 mm  [stored 0.0328084 ft]; Profile_Dia_3=20 mm; Top_Profile=292 mm; Top_Profile_Ref=297 mm; Top_Ref=413.25 mm; Top_Ref_2=431.81 mm; W=510 mm; W_Ref=505 mm
- 879-0250-00-14400239999_DN250_PN16: Body_Collar_Dia=76.04 mm; Body_Collar_Dia_2=65.47 mm; Body_Flange_Dia=235.48 mm; Body_Flange_Dia_2=260.71 mm; Body_Height_1=182.5 mm; Body_Height_2=91.25 mm; Body_Height_3=81 mm; Body_Height_4=106.25 mm; Body_Top_Dia=32.74 mm; Body_Top_Dia_2=27.28 mm; Body_With_Dia=182.5 mm; Body_With_Dia_2=197.3 mm; Bolt_support=486.67 mm; Bolt_support_2=243.33 mm; Bolt_support_Dia=20 mm; Bolt_support_lenght=145.3 mm; Bolt_support_lenght_2=155.3 mm; Bottom_profile=62.65 mm; D1=159.5 mm; DN=250.6 mm; FOD=202.5 mm; Fillet_Length=10 mm  [stored 0.0328084 ft]; Flange_thickness=22 mm; H3=690 mm; ID=125.3 mm; L=730 mm; L1=747 mm; L_Ref=738.5 mm; PG_Dia=83.53 mm; PG_Ref=121.67 mm; PG_depth=14 mm  [stored 0.0459318 ft]; PG_ref=135.3 mm; Pilot_Dia_1=47 mm; Pilot_Dia_2=94 mm; Pilot_Dia_3=31.33 mm; Pilot_Dia_4=15.67 mm; Pilot_Dia_5=10.44 mm; Pilot_top_1=438.63 mm; Pilot_top_ref=48.88 mm; Profile1_Height=335 mm; Profile1_Length=54.73 mm; Profile1_Length_2=36.49 mm; Profile_Dia=10 mm  [stored 0.0328084 ft]; Profile_Dia_2=10 mm  [stored 0.0328084 ft]; Profile_Dia_3=20 mm; Top_Profile=292 mm; Top_Profile_Ref=297 mm; Top_Ref=389.75 mm; Top_Ref_2=414.19 mm; W=510 mm; W_Ref=505 mm
- 879-0250-00-144002399A0_DN250_PN16: Body_Collar_Dia=76.04 mm; Body_Collar_Dia_2=65.47 mm; Body_Flange_Dia=235.48 mm; Body_Flange_Dia_2=260.71 mm; Body_Height_1=182.5 mm; Body_Height_2=91.25 mm; Body_Height_3=81 mm; Body_Height_4=106.25 mm; Body_Top_Dia=32.74 mm; Body_Top_Dia_2=27.28 mm; Body_With_Dia=182.5 mm; Body_With_Dia_2=197.3 mm; Bolt_support=486.67 mm; Bolt_support_2=243.33 mm; Bolt_support_Dia=20 mm; Bolt_support_lenght=145.35 mm; Bolt_support_lenght_2=155.35 mm; Bottom_profile=62.68 mm; D1=159.5 mm; DN=250.7 mm; FOD=202.5 mm; Fillet_Length=10 mm  [stored 0.0328084 ft]; Flange_thickness=22 mm; H3=690 mm; ID=125.35 mm; L=730 mm; L1=747 mm; L_Ref=738.5 mm; PG_Dia=83.57 mm; PG_Ref=121.67 mm; PG_depth=14 mm  [stored 0.0459318 ft]; PG_ref=135.35 mm; Pilot_Dia_1=47 mm; Pilot_Dia_2=94 mm; Pilot_Dia_3=31.33 mm; Pilot_Dia_4=15.67 mm; Pilot_Dia_5=10.44 mm; Pilot_top_1=438.63 mm; Pilot_top_ref=48.88 mm; Profile1_Height=350 mm; Profile1_Length=54.73 mm; Profile1_Length_2=36.49 mm; Profile_Dia=10 mm  [stored 0.0328084 ft]; Profile_Dia_2=10 mm  [stored 0.0328084 ft]; Profile_Dia_3=20 mm; Top_Profile=292 mm; Top_Profile_Ref=297 mm; Top_Ref=389.75 mm; Top_Ref_2=414.19 mm; W=510 mm; W_Ref=505 mm

note: [stored X ft] marks values corroborated as IEEE doubles in the binary element streams (Revit-internal decimal feet)

## geometry (parser evidence)
native form markers: Sweep x3
no freeform markers — native parametric forms only
